# Revit family: Sanitary_Basins_TOTO-USA-Inc_AthertonT-Undercounter-Lavatory
name_source: partatom
category: Plumbing Fixtures
revit_build: Autodesk Revit 2015 (Build: 20140606_1530(x64)
units: mm (PartAtom-declared; Revit-internal decimal feet)

## types (1)
- LT221
    BIMobject category = Basins
    BIMobject category code = sanitary-basins
    BIMobject main category = Sanitary
    BIMobject main category code = sanitary
    Brand url = https://www.totousa.com
    Default Elevation = 1219 mm
    Description = This lavatory offers a rimless, rectangular design and concealed front overflow. Features a generously deep basin with more vertical sides.  ADA compliant.
    Edition number = 1
    Installation instructions = https://www.totousa.com
    Manufacturer = TOTO
    Manufacturer name = TOTO USA Inc
    Masterformat 2014 Code = 22 41 16.16
    Masterformat 2014 Description = Residential Sinks
    Material = Galaline - TOTO - Reinforced Marble
    Material main = Ceramics
    Model = LT221
    Nominal height = 0 mm  [stored 0 ft]
    Nominal width = 0 mm  [stored 0 ft]
    OmniClass Code = 23-31 13 00
    OmniClass Description = Sinks
    Product Guid = 09a74a50-6178-468f-be83-a7c99eec7ae0
    Product SKU = toto-lt221
    Product certification = https://www.totousa.com
    Product data url = https://bimobject.com
    Product family = Sinks/Lavatories
    Product group = Atherton???
    Product url = https://www.totousa.com
    QR code = http://bimobject.com
    Technical description = https://www.totousa.com
    UNSPSC Code = 30181504
    URL = https://www.totousa.com
    Uniclass 1.4 Code = L72331
    Uniclass 1.4 Description = Sinks, troughs
    Uniclass 2.0 Code = PR-31-79
    Uniclass 2.0 Description = Sinks, Wash Basins And Troughs
    Uniclass 2015 Code = Pr_40_20_96_81
    Uniclass 2015 Name = Sinks
    Uniformat II Code = D2030
    Uniformat II Description = Sanitary Waste

note: [stored X ft] marks values corroborated as IEEE doubles in the binary element streams (Revit-internal decimal feet)

## geometry (parser evidence)
native form markers: Blend x4, Sweep x2
no freeform markers — native parametric forms only
